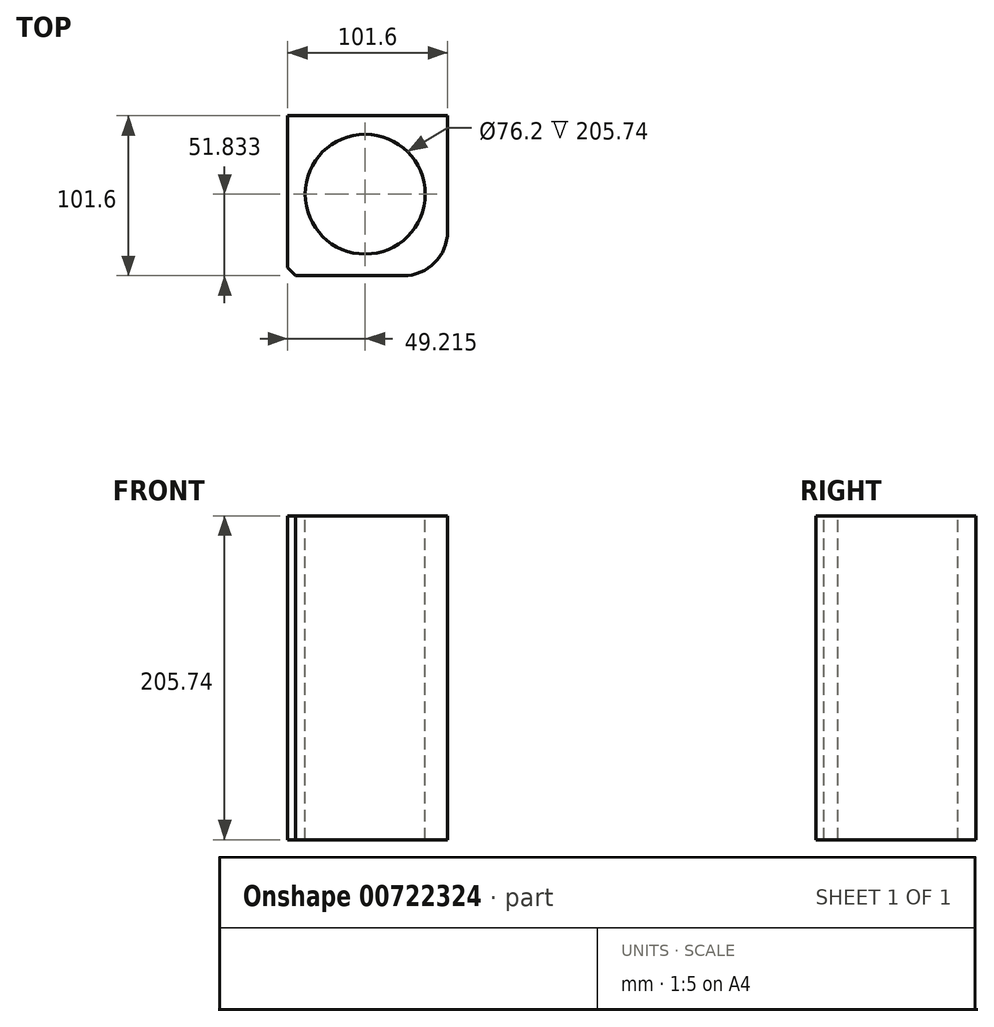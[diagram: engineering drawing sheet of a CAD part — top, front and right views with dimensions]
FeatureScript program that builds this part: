
annotation { "Feature Type Name" : "Feature", "Feature Type Description" : "" }
export const myFeature = defineFeature(function(context is Context, id is Id, definition is map)
    precondition{}
    {
        {
            var Q0;
            Q0=qCreatedBy(makeId("Top.planeOp"),FACE);
            var sketch = newSketch(context, id + "F0", { "sketchPlane" : qUnion([Q0])});
            skLineSegment(sketch, "E0", {"start": v(0, 0) * mm, "end": v(0, 101.6) * mm});
            skLineSegment(sketch, "E1", {"start": v(0, 101.6) * mm, "end": v(101.6, 101.6) * mm});
            skLineSegment(sketch, "E2", {"start": v(101.6, 101.6) * mm, "end": v(101.6, 0) * mm});
            skLineSegment(sketch, "E3", {"start": v(0, 0) * mm, "end": v(101.6, 0) * mm});
            skSolve(sketch);
        }
        {
            var Q0;
            Q0 = qSketchRegion(id + "F0", true);
            extrude(context, id + "F1", {"entities" : qUnion([Q0]), "depth" : 205.74 * mm, "offsetDistance" : 25.4 * mm});
        }
        {
            var Q0;
            Q0=makeQuery(id+"F1.opExtrude","CAP_FACE",FACE,{"disambiguationData":[OSD([sQuery(id+"F0.wireOp",EDGE,"E0"),sQuery(id+"F0.wireOp",EDGE,"E1"),sQuery(id+"F0.wireOp",EDGE,"E2"),sQuery(id+"F0.wireOp",EDGE,"E3")])],"isStart":false});
            var sketch = newSketch(context, id + "F2", { "sketchPlane" : qUnion([Q0])});
            skSolve(sketch);
        }
        {
            var Q0;
            Q0=makeQuery(id+"F2.imprint","IMPRINT",FACE,{"disambiguationData":[TD([[makeQuery(id+"F2.imprint","IMPRINT",EDGE,{"derivedFrom":makeQuery(id+"F1.opExtrude","CAP_EDGE",EDGE,{"disambiguationData":[OSD([sQuery(id+"F0.wireOp",EDGE,"E0")])],"isStart":false})}),-1.0]])]});
            var sketch = newSketch(context, id + "F3", { "sketchPlane" : qUnion([Q0])});
            skCircle(sketch, "E4", {"center": v(49.22, 51.83) * mm, "radius": 38.1 * mm});
            skSolve(sketch);
        }
        {
            var Q0;
            Q0 = qSketchRegion(id + "F3", true);
            extrude(context, id + "F4", {"entities" : qUnion([Q0]), "operationType" : NewBodyOperationType.REMOVE, "endBound" : BoundingType.THROUGH_ALL, "oppositeDirection" : true, "depth" : 25.4 * mm, "offsetDistance" : 25.4 * mm});
        }
        {
            var Q0;
            Q0=makeQuery(id+"F1.opExtrude","SWEPT_EDGE",EDGE,{"disambiguationData":[OSD([sQuery(id+"F0.wireOp",EDGE,"E2"),sQuery(id+"F0.wireOp",EDGE,"E3")])]});
            fillet(context, id + "F5", {"entities" : qUnion([Q0]), "radius" : 28.2 * mm, "tangentPropagation" : true, "allowEdgeOverflow" : false});
        }
        {
            var Q0;
            Q0=makeQuery(id+"F1.opExtrude","SWEPT_EDGE",EDGE,{"disambiguationData":[OSD([sQuery(id+"F0.wireOp",EDGE,"E0"),sQuery(id+"F0.wireOp",EDGE,"E3")])]});
            chamfer(context, id + "F6", {"entities" : qUnion([Q0]), "width" : 5.08 * mm, "tangentPropagation" : true});
        }
    });
